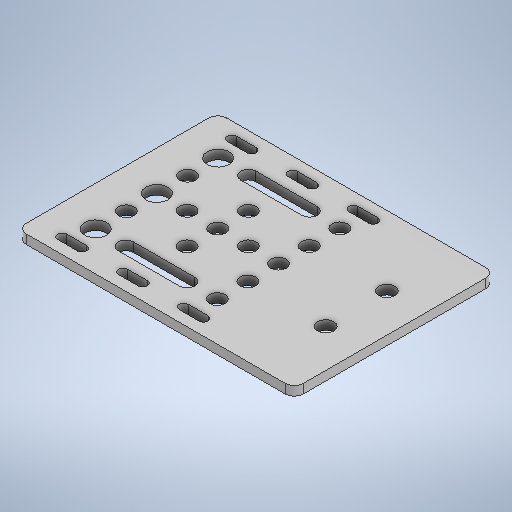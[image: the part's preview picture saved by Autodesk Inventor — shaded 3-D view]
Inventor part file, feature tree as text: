
AUTODESK INVENTOR PART (.ipt)
format: ipt  version: 2025.2 (Build 292293000, 293)  size: 326,656 bytes
history: native  units: in
note: dims shown in document units (in); Inventor stores cm internally (conversion verified against a paired STEP export)
features: extrude x1, fillet x1, sketch x1
ambient origin geometry x8: Origin, YZ Plane, XZ Plane, XY Plane, X Axis, Y Axis, Z Axis, Center Point
bodies: Solid1 (feature_tree), Body1 (feature_tree)
feature tree (3):
  extrude  "Extrusion1"  Depth=0.1181in TaperAngle=0.0deg
  fillet  "Fillet1"  Radius=0.1181in
  sketch  "Sketch1"  dims[d5=0.9843in d7=0.1181in d8=0.0in d9=0.1181in d10=0.3937in d11=0.3937in d12=0.2087in d13=0.2087in]
